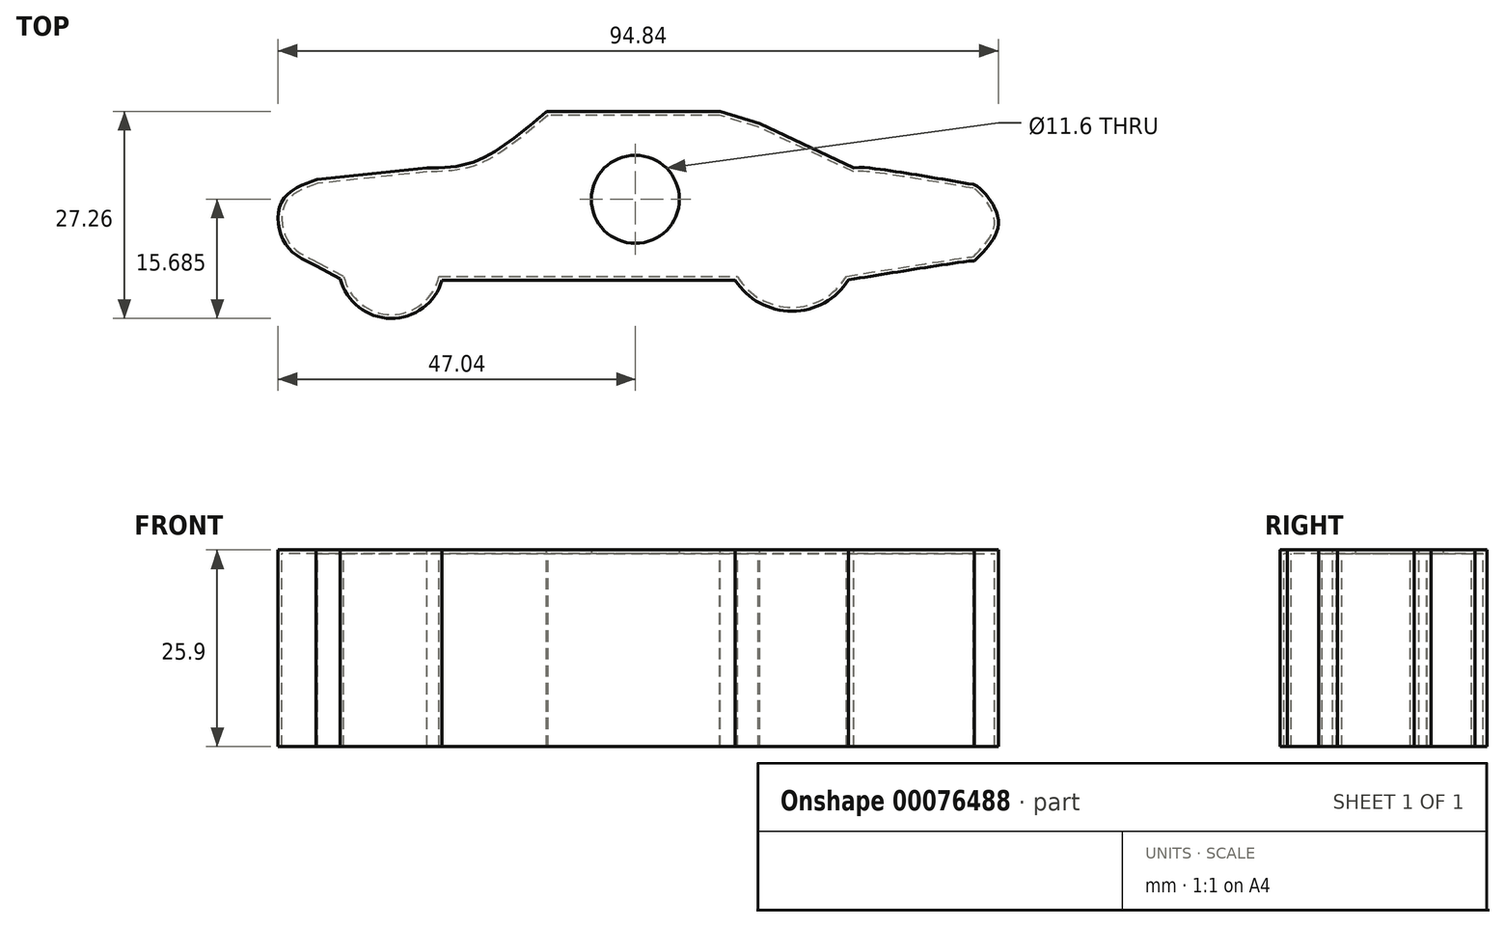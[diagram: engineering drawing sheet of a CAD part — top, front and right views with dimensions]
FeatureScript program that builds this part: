
annotation { "Feature Type Name" : "Feature", "Feature Type Description" : "" }
export const myFeature = defineFeature(function(context is Context, id is Id, definition is map)
    precondition{}
    {
        {
            var Q0;
            Q0=qCreatedBy(makeId("Top.planeOp"),FACE);
            var sketch = newSketch(context, id + "F0", { "sketchPlane" : qUnion([Q0])});
            skLineSegment(sketch, "E0", {"start": v(-25.84, -7.78) * mm, "end": v(11.28, -7.78) * mm});
            skLineSegment(sketch, "E1", {"start": v(11.28, -7.78) * mm, "end": v(13.44, -7.78) * mm});
            skArc(sketch, "E2", {"start": v(-38.4, -7.78) * mm, "mid": v(-32.12, -12.83) * mm, "end": v(-25.84, -7.78) * mm});
            skArc(sketch, "E3", {"start": v(13.44, -7.78) * mm, "mid": v(20.61, -11.88) * mm, "end": v(27.78, -7.78) * mm});
            skFitSpline(sketch, "E4", {"points": [v(27.78, -7.78) * mm, v(44.28, -5.23) * mm, v(44.48, -5.23) * mm], "startDerivative": vector(25.63, 4.1) * mm, "endDerivative": vector(1.21, -0.14) * mm});
            skFitSpline(sketch, "E5", {"points": [v(44.48, -5.23) * mm, v(47.23, 0) * mm, v(44.48, 3.8) * mm, v(44.48, 3.41) * mm], "startDerivative": vector(10.3, 10.44) * mm, "endDerivative": vector(1.18, -4.75) * mm});
            skFitSpline(sketch, "E6", {"points": [v(44.48, 3.8) * mm, v(28.76, 5.96) * mm, v(28.76, 5.77) * mm], "startDerivative": vector(-25.32, 4.36) * mm, "endDerivative": vector(0.87, -2.18) * mm});
            skFitSpline(sketch, "E7", {"points": [v(28.76, 5.96) * mm, v(16.2, 11.86) * mm], "startDerivative": vector(-12.57, 5.9) * mm, "endDerivative": vector(-12.57, 5.9) * mm});
            skFitSpline(sketch, "E8", {"points": [v(16.2, 11.86) * mm, v(11.09, 13.43) * mm], "startDerivative": vector(-5.1, 1.57) * mm, "endDerivative": vector(-5.1, 1.57) * mm});
            skFitSpline(sketch, "E9", {"points": [v(11.09, 13.43) * mm, v(-11.5, 13.43) * mm], "startDerivative": vector(-22.59, 0) * mm, "endDerivative": vector(-22.59, 0) * mm});
            skFitSpline(sketch, "E10", {"points": [v(-11.5, 13.43) * mm, v(-20.73, 6.95) * mm, v(-27.41, 5.96) * mm], "startDerivative": vector(-16.67, -14.1) * mm, "endDerivative": vector(-15.08, -0.24) * mm});
            skFitSpline(sketch, "E11", {"points": [v(-27.41, 5.96) * mm, v(-41.82, 4.45) * mm], "startDerivative": vector(-14.4, -1.52) * mm, "endDerivative": vector(-14.4, -1.52) * mm});
            skFitSpline(sketch, "E12", {"points": [v(-41.82, 4.45) * mm, v(-46.08, 1.85) * mm, v(-45.71, -3.15) * mm, v(-41.82, -5.94) * mm], "startDerivative": vector(-15.67, -5.4) * mm, "endDerivative": vector(13.78, -6.3) * mm});
            skFitSpline(sketch, "E13", {"points": [v(-41.82, -5.94) * mm, v(-38.4, -7.78) * mm], "startDerivative": vector(3.41, -1.85) * mm, "endDerivative": vector(3.41, -1.85) * mm});
            skSolve(sketch);
        }
        {
            var Q0;
            Q0=makeQuery(id+"F0.imprint","IMPRINT",FACE,{"disambiguationData":[TD([[makeQuery(id+"F0.imprint","IMPRINT",EDGE,{"derivedFrom":sQuery(id+"F0.wireOp",EDGE,"E0")}),1.0]])]});
            extrude(context, id + "F1", {"entities" : qUnion([Q0]), "oppositeDirection" : true, "depth" : 25.4 * mm});
        }
        {
            var Q0;
            Q0=makeQuery(id+"F1.opExtrude","CAP_FACE",FACE,{"disambiguationData":[OSD([sQuery(id+"F0.wireOp",EDGE,"E0"),sQuery(id+"F0.wireOp",EDGE,"E1"),sQuery(id+"F0.wireOp",EDGE,"E2"),sQuery(id+"F0.wireOp",EDGE,"E3"),sQuery(id+"F0.wireOp",EDGE,"E4"),sQuery(id+"F0.wireOp",EDGE,"E5"),sQuery(id+"F0.wireOp",EDGE,"E6"),sQuery(id+"F0.wireOp",EDGE,"E7"),sQuery(id+"F0.wireOp",EDGE,"E8"),sQuery(id+"F0.wireOp",EDGE,"E9"),sQuery(id+"F0.wireOp",EDGE,"E10"),sQuery(id+"F0.wireOp",EDGE,"E11"),sQuery(id+"F0.wireOp",EDGE,"E12"),sQuery(id+"F0.wireOp",EDGE,"E13")])],"isStart":false});
            shell(context, id + "F2", {"entities" : qUnion([Q0]), "thickness" : .5 * mm, "oppositeDirection" : true});
        }
        {
            var Q0;
            Q0=qCreatedBy(makeId("Top.planeOp"),FACE);
            var sketch = newSketch(context, id + "F3", { "sketchPlane" : qUnion([Q0])});
            skCircle(sketch, "E14", {"center": v(0, 2.36) * mm, "radius": 5.8 * mm});
            skSolve(sketch);
        }
        {
            var Q0;
            Q0=makeQuery(id+"F3.imprint","IMPRINT",FACE,{"disambiguationData":[TD([[makeQuery(id+"F3.imprint","IMPRINT",EDGE,{"derivedFrom":sQuery(id+"F3.wireOp",EDGE,"E14")}),1.0]])]});
            var Q1;
            Q1=sQuery(id+"F3.wireOp",EDGE,"E14");
            extrude(context, id + "F4", {"entities" : qUnion([Q0]), "operationType" : NewBodyOperationType.REMOVE, "surfaceEntities" : qUnion([Q1]), "depth" : 69.23 * mm});
        }
    });
